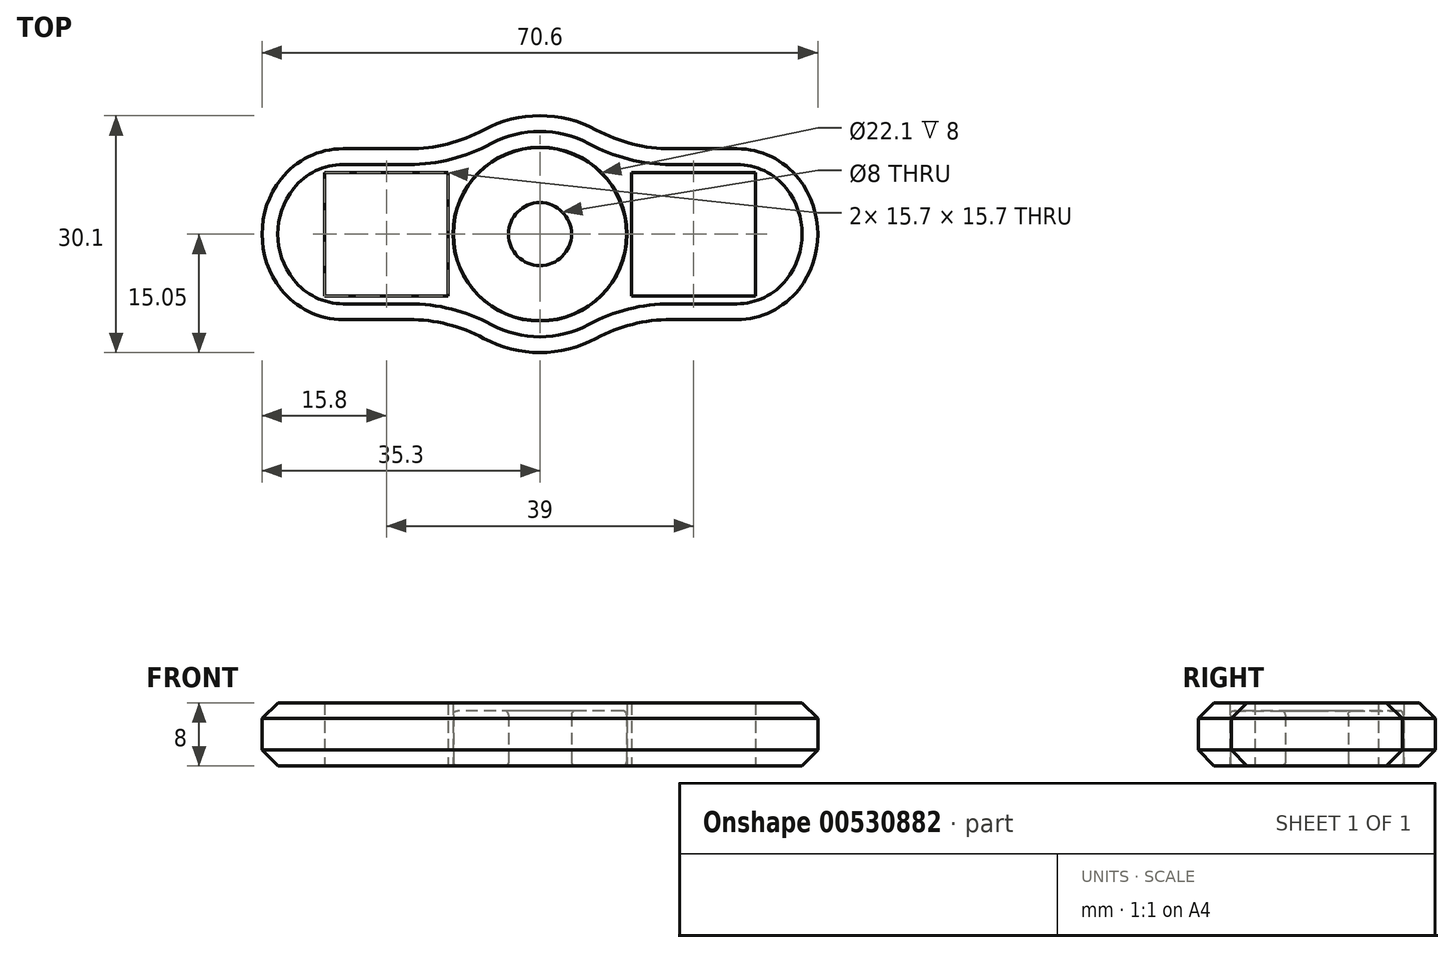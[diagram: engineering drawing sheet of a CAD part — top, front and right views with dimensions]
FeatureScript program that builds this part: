
annotation { "Feature Type Name" : "Feature", "Feature Type Description" : "" }
export const myFeature = defineFeature(function(context is Context, id is Id, definition is map)
    precondition{}
    {
        {
            var Q0;
            Q0=qCreatedBy(makeId("Top.planeOp"),FACE);
            var sketch = newSketch(context, id + "F0", { "sketchPlane" : qUnion([Q0])});
            skCircle(sketch, "E0", {"center": v(0, 0) * mm, "radius": 11 * mm});
            skCircle(sketch, "E1", {"center": v(0, 0) * mm, "radius": 4 * mm});
            skSolve(sketch);
        }
        {
            var Q0;
            Q0=makeQuery(id+"F0.imprint","IMPRINT",FACE,{"disambiguationData":[TD([[makeQuery(id+"F0.imprint","IMPRINT",EDGE,{"derivedFrom":sQuery(id+"F0.wireOp",EDGE,"E0")}),1.0]])]});
            extrude(context, id + "F1", {"entities" : qUnion([Q0]), "depth" : 7 * mm, "offsetDistance" : 25 * mm});
        }
        {
            var Q0;
            Q0=makeQuery(id+"F1.opExtrude","CAP_FACE",FACE,{"disambiguationData":[OSD([sQuery(id+"F0.wireOp",EDGE,"E0"),sQuery(id+"F0.wireOp",EDGE,"E1")])],"isStart":true});
            var sketch = newSketch(context, id + "F2", { "sketchPlane" : qUnion([Q0])});
            skCircle(sketch, "E2.0", {"center": v(0, 0) * mm, "radius": 11.05 * mm});
            skCircle(sketch, "E3.0", {"center": v(0, 0) * mm, "radius": 15.05 * mm});
            skLineSegment(sketch, "E4", {"start": v(0, 0) * mm, "end": v(-19.5, 0) * mm, "construction": true});
            skLineSegment(sketch, "E5.bottom", {"start": v(-27.35, -7.85) * mm, "end": v(-11.65, -7.85) * mm});
            skLineSegment(sketch, "E5.top", {"start": v(-27.35, 7.85) * mm, "end": v(-11.65, 7.85) * mm});
            skLineSegment(sketch, "E5.left", {"start": v(-27.35, -7.85) * mm, "end": v(-27.35, 7.85) * mm});
            skLineSegment(sketch, "E5.right", {"start": v(-11.65, -7.85) * mm, "end": v(-11.65, 7.85) * mm});
            skPoint(sketch, "E5.middle", {"position": v(-19.5, 0) * mm});
            skCircle(sketch, "E6", {"center": v(0, 0) * mm, "radius": 50 * mm, "construction": true});
            skLineSegment(sketch, "E7", {"start": v(-19.5, 0) * mm, "end": v(-35.3, 0) * mm, "construction": true});
            skLineSegment(sketch, "E8", {"start": v(-27.35, 7.85) * mm, "end": v(-27.35, 10.85) * mm, "construction": true});
            skLineSegment(sketch, "E9.0", {"start": v(-23, 10.85) * mm, "end": v(-27.35, 10.85) * mm});
            skLineSegment(sketch, "E9.1", {"start": v(0, 10.85) * mm, "end": v(-2.1, 10.85) * mm, "construction": true});
            skLineSegment(sketch, "E10.trimOffspring", {"start": v(-10.43, 10.85) * mm, "end": v(-23, 10.85) * mm});
            skLineSegment(sketch, "E11.MirrorCS", {"start": v(-10.43, -10.85) * mm, "end": v(-23, -10.85) * mm});
            skLineSegment(sketch, "E12.MirrorCS", {"start": v(-23, -10.85) * mm, "end": v(-27.35, -10.85) * mm});
            skArc(sketch, "E13", {"start": v(-27.35, 10.85) * mm, "mid": v(-35.3, 0) * mm, "end": v(-27.35, -10.85) * mm});
            skLineSegment(sketch, "E14.1.0", {"start": v(27.35, 7.85) * mm, "end": v(11.65, 7.85) * mm});
            skLineSegment(sketch, "E14.1.1", {"start": v(11.65, 7.85) * mm, "end": v(11.65, -7.85) * mm});
            skLineSegment(sketch, "E14.1.2", {"start": v(27.35, -7.85) * mm, "end": v(11.65, -7.85) * mm});
            skLineSegment(sketch, "E14.1.3", {"start": v(10.43, -10.85) * mm, "end": v(23, -10.85) * mm});
            skLineSegment(sketch, "E14.1.4", {"start": v(23, -10.85) * mm, "end": v(27.35, -10.85) * mm});
            skLineSegment(sketch, "E14.1.5", {"start": v(27.35, 7.85) * mm, "end": v(27.35, -7.85) * mm});
            skArc(sketch, "E14.1.6", {"start": v(27.35, -10.85) * mm, "mid": v(35.3, 0) * mm, "end": v(27.35, 10.85) * mm});
            skLineSegment(sketch, "E14.1.7", {"start": v(23, 10.85) * mm, "end": v(27.35, 10.85) * mm});
            skLineSegment(sketch, "E14.1.8", {"start": v(10.43, 10.85) * mm, "end": v(23, 10.85) * mm});
            skCircle(sketch, "E15", {"center": v(0, 0) * mm, "radius": 29.42 * mm, "construction": true});
            skSolve(sketch);
        }
        {
            var Q0;
            Q0=makeQuery(id+"F1.opExtrude","CAP_FACE",FACE,{"disambiguationData":[OSD([sQuery(id+"F0.wireOp",EDGE,"E0"),sQuery(id+"F0.wireOp",EDGE,"E1")])],"isStart":true});
            var Q1;
            Q1=makeQuery(id+"F1.opExtrude","CAP_FACE",FACE,{"disambiguationData":[OSD([sQuery(id+"F0.wireOp",EDGE,"E0"),sQuery(id+"F0.wireOp",EDGE,"E1")])],"isStart":false});
            fillet(context, id + "F3", {"entities" : qUnion([Q0, Q1]), "radius" : .5 * mm, "tangentPropagation" : true, "allowEdgeOverflow" : false});
        }
        {
            var Q0;
            {var subQ5=sQuery(id+"F2.wireOp",EDGE,"E14.2.0");Q0=makeQuery(id+"F2.imprint","IMPRINT",FACE,{"disambiguationData":[TD([[makeQuery(id+"F2.imprint","IMPRINT",EDGE,{"derivedFrom":subQ5}),-1.0]])]});}
            var Q1;
            Q1=makeQuery(id+"F2.imprint","IMPRINT",FACE,{"disambiguationData":[TD([[makeQuery(id+"F2.imprint","IMPRINT",EDGE,{"derivedFrom":sQuery(id+"F2.wireOp",EDGE,"E2.0")}),-1.0]])]});
            var Q2;
            {var subQ6=sQuery(id+"F2.wireOp",EDGE,"E14.1.0");Q2=makeQuery(id+"F2.imprint","IMPRINT",FACE,{"disambiguationData":[TD([[makeQuery(id+"F2.imprint","IMPRINT",EDGE,{"derivedFrom":subQ6}),-1.0]])]});}
            var Q3;
            {var subQ5=sQuery(id+"F2.wireOp",EDGE,"E5.bottom");Q3=makeQuery(id+"F2.imprint","IMPRINT",FACE,{"disambiguationData":[TD([[makeQuery(id+"F2.imprint","IMPRINT",EDGE,{"derivedFrom":subQ5}),-1.0]])]});}
            extrude(context, id + "F4", {"entities" : qUnion([Q0, Q1, Q2, Q3]), "oppositeDirection" : true, "depth" : 8 * mm, "offsetDistance" : 25 * mm});
        }
        {
            var Q0;
            Q0=makeQuery(id+"F4.opExtrude","SWEPT_EDGE",EDGE,{"disambiguationData":[OSD([sQuery(id+"F2.wireOp",EDGE,"E3.0"),sQuery(id+"F2.wireOp",EDGE,"E14.2.3")])]});
            var Q1;
            Q1=makeQuery(id+"F4.opExtrude","SWEPT_EDGE",EDGE,{"disambiguationData":[OSD([sQuery(id+"F2.wireOp",EDGE,"E3.0"),sQuery(id+"F2.wireOp",EDGE,"E14.1.8")])]});
            var Q2;
            Q2=makeQuery(id+"F4.opExtrude","SWEPT_EDGE",EDGE,{"disambiguationData":[OSD([sQuery(id+"F2.wireOp",EDGE,"E3.0"),sQuery(id+"F2.wireOp",EDGE,"E14.2.8")])]});
            var Q3;
            Q3=makeQuery(id+"F4.opExtrude","SWEPT_EDGE",EDGE,{"disambiguationData":[OSD([sQuery(id+"F2.wireOp",EDGE,"E3.0"),sQuery(id+"F2.wireOp",EDGE,"E10.trimOffspring")])]});
            var Q4;
            Q4=makeQuery(id+"F4.opExtrude","SWEPT_EDGE",EDGE,{"disambiguationData":[OSD([sQuery(id+"F2.wireOp",EDGE,"E3.0"),sQuery(id+"F2.wireOp",EDGE,"E11.MirrorCS")])]});
            var Q5;
            Q5=makeQuery(id+"F4.opExtrude","SWEPT_EDGE",EDGE,{"disambiguationData":[OSD([sQuery(id+"F2.wireOp",EDGE,"E3.0"),sQuery(id+"F2.wireOp",EDGE,"E14.1.3")])]});
            fillet(context, id + "F5", {"entities" : qUnion([Q0, Q1, Q2, Q3, Q4, Q5]), "radius" : 20 * mm, "tangentPropagation" : true, "allowEdgeOverflow" : false});
        }
        {
            var Q0;
            Q0=makeQuery(id+"F4.opExtrude","SWEPT_EDGE",EDGE,{"disambiguationData":[OSD([sQuery(id+"F2.wireOp",EDGE,"E14.2.4"),sQuery(id+"F2.wireOp",EDGE,"E14.2.6")])]});
            var Q1;
            Q1=makeQuery(id+"F4.opExtrude","SWEPT_EDGE",EDGE,{"disambiguationData":[OSD([sQuery(id+"F2.wireOp",EDGE,"E14.2.6"),sQuery(id+"F2.wireOp",EDGE,"E14.2.7")])]});
            var Q2;
            Q2=makeQuery(id+"F4.opExtrude","SWEPT_EDGE",EDGE,{"disambiguationData":[OSD([sQuery(id+"F2.wireOp",EDGE,"E9.0"),sQuery(id+"F2.wireOp",EDGE,"E13")])]});
            var Q3;
            Q3=makeQuery(id+"F4.opExtrude","SWEPT_EDGE",EDGE,{"disambiguationData":[OSD([sQuery(id+"F2.wireOp",EDGE,"E12.MirrorCS"),sQuery(id+"F2.wireOp",EDGE,"E13")])]});
            var Q4;
            Q4=makeQuery(id+"F4.opExtrude","SWEPT_EDGE",EDGE,{"disambiguationData":[OSD([sQuery(id+"F2.wireOp",EDGE,"E14.1.4"),sQuery(id+"F2.wireOp",EDGE,"E14.1.6")])]});
            var Q5;
            Q5=makeQuery(id+"F4.opExtrude","SWEPT_EDGE",EDGE,{"disambiguationData":[OSD([sQuery(id+"F2.wireOp",EDGE,"E14.1.6"),sQuery(id+"F2.wireOp",EDGE,"E14.1.7")])]});
            fillet(context, id + "F6", {"entities" : qUnion([Q0, Q1, Q2, Q3, Q4, Q5]), "radius" : 10 * mm, "tangentPropagation" : true, "allowEdgeOverflow" : false});
        }
        {
            var Q0;
            Q0=makeQuery(id+"F4.opExtrude","CAP_EDGE",EDGE,{"disambiguationData":[OSD([sQuery(id+"F2.wireOp",EDGE,"E14.2.6")])],"isStart":false});
            var Q1;
            Q1=makeQuery(id+"F4.opExtrude","CAP_EDGE",EDGE,{"disambiguationData":[OSD([sQuery(id+"F2.wireOp",EDGE,"E14.1.6")])],"isStart":false});
            var Q2;
            {var subQ0=sQuery(id+"F2.wireOp",EDGE,"E13");var subQ1=sQuery(id+"F2.wireOp",EDGE,"E9.0");Q2=makeQuery(id+"F6.opFillet","BLEND_EDGE",EDGE,{"blendedFrom":[makeQuery(id+"F4.opExtrude","SWEPT_EDGE",EDGE,{"disambiguationData":[OSD([subQ1,subQ0])]}),makeQuery(id+"F4.opExtrude","CAP_FACE",FACE,{"disambiguationData":[OSD([sQuery(id+"F2.wireOp",EDGE,"E2.0"),sQuery(id+"F2.wireOp",EDGE,"E3.0"),sQuery(id+"F2.wireOp",EDGE,"E5.bottom"),sQuery(id+"F2.wireOp",EDGE,"E5.top"),sQuery(id+"F2.wireOp",EDGE,"E5.left"),sQuery(id+"F2.wireOp",EDGE,"E5.right"),subQ1,sQuery(id+"F2.wireOp",EDGE,"E10.trimOffspring"),sQuery(id+"F2.wireOp",EDGE,"E11.MirrorCS"),sQuery(id+"F2.wireOp",EDGE,"E12.MirrorCS"),subQ0,sQuery(id+"F2.wireOp",EDGE,"E14.1.0"),sQuery(id+"F2.wireOp",EDGE,"E14.1.1"),sQuery(id+"F2.wireOp",EDGE,"E14.1.2"),sQuery(id+"F2.wireOp",EDGE,"E14.1.3"),sQuery(id+"F2.wireOp",EDGE,"E14.1.4"),sQuery(id+"F2.wireOp",EDGE,"E14.1.5"),sQuery(id+"F2.wireOp",EDGE,"E14.1.6"),sQuery(id+"F2.wireOp",EDGE,"E14.1.7"),sQuery(id+"F2.wireOp",EDGE,"E14.1.8"),sQuery(id+"F2.wireOp",EDGE,"E14.2.0"),sQuery(id+"F2.wireOp",EDGE,"E14.2.1"),sQuery(id+"F2.wireOp",EDGE,"E14.2.2"),sQuery(id+"F2.wireOp",EDGE,"E14.2.3"),sQuery(id+"F2.wireOp",EDGE,"E14.2.4"),sQuery(id+"F2.wireOp",EDGE,"E14.2.5"),sQuery(id+"F2.wireOp",EDGE,"E14.2.6"),sQuery(id+"F2.wireOp",EDGE,"E14.2.7"),sQuery(id+"F2.wireOp",EDGE,"E14.2.8")])],"isStart":false})],"blendedInto":[makeQuery(id+"F4.opExtrude","CAP_FACE",FACE,{"disambiguationData":[OSD([sQuery(id+"F2.wireOp",EDGE,"E2.0"),sQuery(id+"F2.wireOp",EDGE,"E3.0"),sQuery(id+"F2.wireOp",EDGE,"E5.bottom"),sQuery(id+"F2.wireOp",EDGE,"E5.top"),sQuery(id+"F2.wireOp",EDGE,"E5.left"),sQuery(id+"F2.wireOp",EDGE,"E5.right"),subQ1,sQuery(id+"F2.wireOp",EDGE,"E10.trimOffspring"),sQuery(id+"F2.wireOp",EDGE,"E11.MirrorCS"),sQuery(id+"F2.wireOp",EDGE,"E12.MirrorCS"),subQ0,sQuery(id+"F2.wireOp",EDGE,"E14.1.0"),sQuery(id+"F2.wireOp",EDGE,"E14.1.1"),sQuery(id+"F2.wireOp",EDGE,"E14.1.2"),sQuery(id+"F2.wireOp",EDGE,"E14.1.3"),sQuery(id+"F2.wireOp",EDGE,"E14.1.4"),sQuery(id+"F2.wireOp",EDGE,"E14.1.5"),sQuery(id+"F2.wireOp",EDGE,"E14.1.6"),sQuery(id+"F2.wireOp",EDGE,"E14.1.7"),sQuery(id+"F2.wireOp",EDGE,"E14.1.8"),sQuery(id+"F2.wireOp",EDGE,"E14.2.0"),sQuery(id+"F2.wireOp",EDGE,"E14.2.1"),sQuery(id+"F2.wireOp",EDGE,"E14.2.2"),sQuery(id+"F2.wireOp",EDGE,"E14.2.3"),sQuery(id+"F2.wireOp",EDGE,"E14.2.4"),sQuery(id+"F2.wireOp",EDGE,"E14.2.5"),sQuery(id+"F2.wireOp",EDGE,"E14.2.6"),sQuery(id+"F2.wireOp",EDGE,"E14.2.7"),sQuery(id+"F2.wireOp",EDGE,"E14.2.8")])],"isStart":false})]});}
            var Q3;
            Q3=makeQuery(id+"F4.opExtrude","CAP_EDGE",EDGE,{"disambiguationData":[OSD([sQuery(id+"F2.wireOp",EDGE,"E14.2.6")])],"isStart":true});
            var Q4;
            Q4=makeQuery(id+"F4.opExtrude","CAP_EDGE",EDGE,{"disambiguationData":[OSD([sQuery(id+"F2.wireOp",EDGE,"E13")])],"isStart":true});
            var Q5;
            Q5=makeQuery(id+"F4.opExtrude","CAP_EDGE",EDGE,{"disambiguationData":[OSD([sQuery(id+"F2.wireOp",EDGE,"E14.1.6")])],"isStart":true});
            chamfer(context, id + "F7", {"entities" : qUnion([Q0, Q1, Q2, Q3, Q4, Q5]), "width" : 2 * mm, "tangentPropagation" : true});
        }
    });
